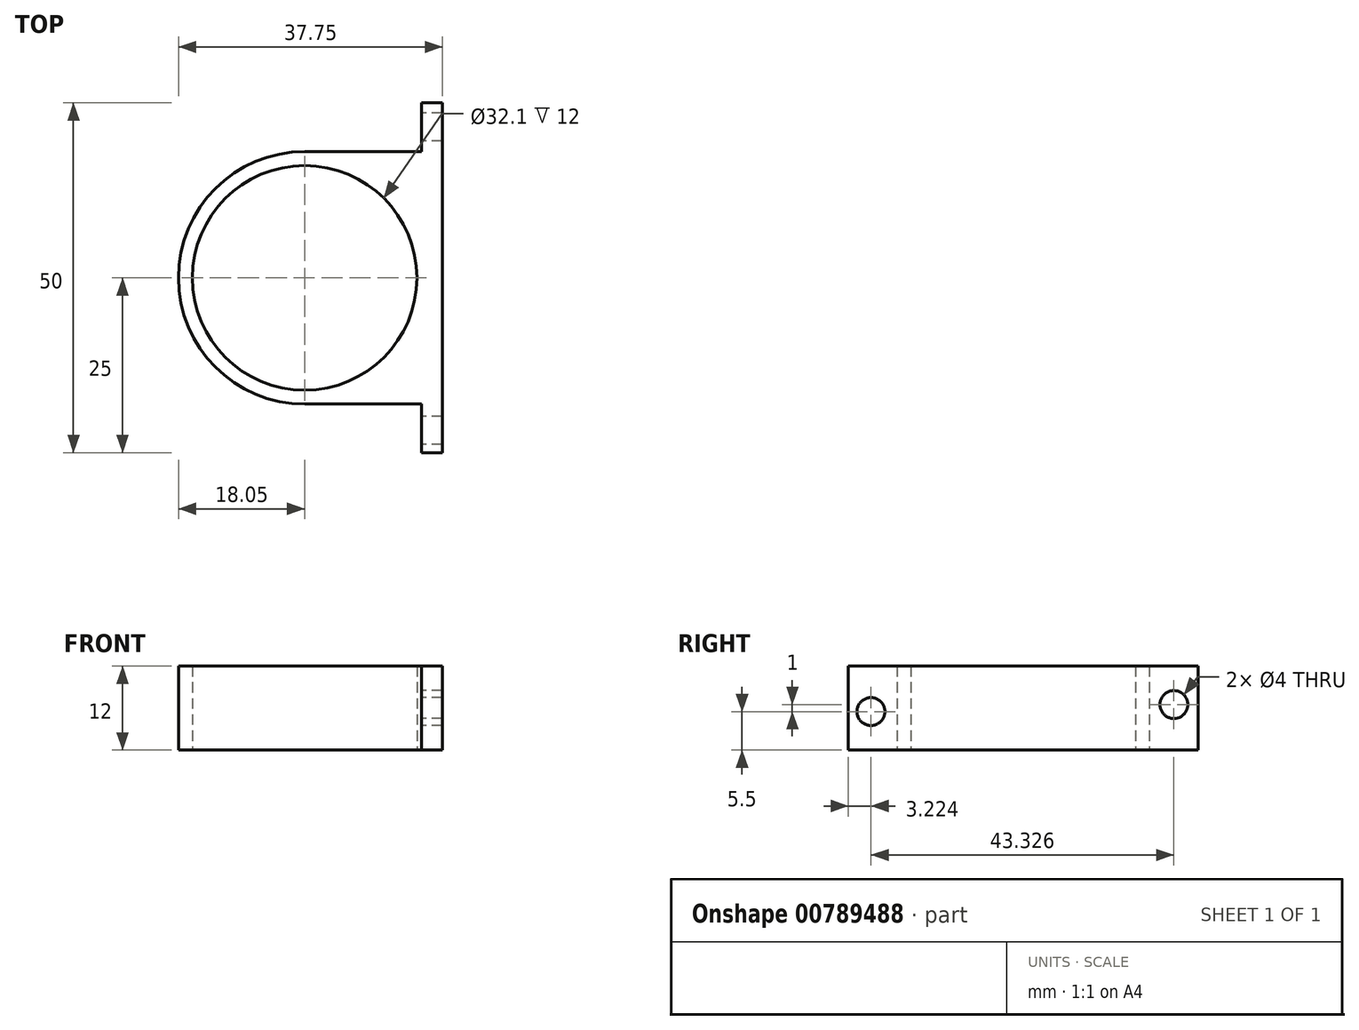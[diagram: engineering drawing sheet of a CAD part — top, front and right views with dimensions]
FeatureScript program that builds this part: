
annotation { "Feature Type Name" : "Feature", "Feature Type Description" : "" }
export const myFeature = defineFeature(function(context is Context, id is Id, definition is map)
    precondition{}
    {
        {
            var Q0;
            Q0=qCreatedBy(makeId("Top.planeOp"),FACE);
            var sketch = newSketch(context, id + "F0", { "sketchPlane" : qUnion([Q0])});
            skCircle(sketch, "E0", {"center": v(0, 0) * mm, "radius": 16.05 * mm});
            skCircle(sketch, "E1.0", {"center": v(0, 0) * mm, "radius": 18.05 * mm});
            skPoint(sketch, "E2", {"position": v(0, 18.05) * mm});
            skPoint(sketch, "E3", {"position": v(0, -18.05) * mm});
            skPoint(sketch, "E4", {"position": v(19.7, 0) * mm});
            skLineSegment(sketch, "E5", {"start": v(19.7, 0) * mm, "end": v(19.7, 25) * mm});
            skLineSegment(sketch, "E6", {"start": v(19.7, 25) * mm, "end": v(16.7, 25) * mm});
            skLineSegment(sketch, "E7", {"start": v(0, 18.05) * mm, "end": v(16.72, 18.05) * mm});
            skLineSegment(sketch, "E8", {"start": v(16.72, 18.05) * mm, "end": v(16.7, 25) * mm});
            skLineSegment(sketch, "E9.MirrorCS", {"start": v(19.7, 0) * mm, "end": v(19.7, -25) * mm});
            skLineSegment(sketch, "E10.MirrorCS", {"start": v(0, -18.05) * mm, "end": v(16.72, -18.05) * mm});
            skLineSegment(sketch, "E11.MirrorCS", {"start": v(16.72, -18.05) * mm, "end": v(16.7, -25) * mm});
            skLineSegment(sketch, "E12.MirrorCS", {"start": v(19.7, -25) * mm, "end": v(16.7, -25) * mm});
            skSolve(sketch);
        }
        {
            var Q0;
            Q0=makeQuery(id+"F0.imprint","IMPRINT",FACE,{"disambiguationData":[TD([[makeQuery(id+"F0.imprint","IMPRINT",EDGE,{"derivedFrom":sQuery(id+"F0.wireOp",EDGE,"E0")}),-1.0]])]});
            var Q1;
            Q1=makeQuery(id+"F0.imprint","IMPRINT",FACE,{"disambiguationData":[TD([[makeQuery(id+"F0.imprint","IMPRINT",EDGE,{"derivedFrom":sQuery(id+"F0.wireOp",EDGE,"E5")}),1.0]])]});
            extrude(context, id + "F1", {"entities" : qUnion([Q0, Q1]), "depth" : 12 * mm, "offsetDistance" : 25 * mm});
        }
        {
            var Q0;
            Q0=makeQuery(id+"F1.opExtrude","SWEPT_FACE",FACE,{"disambiguationData":[OSD([sQuery(id+"F0.wireOp",EDGE,"E11.MirrorCS")])]});
            var sketch = newSketch(context, id + "F2", { "sketchPlane" : qUnion([Q0])});
            skLineSegment(sketch, "E13.bottom", {"start": v(24.96, 0) * mm, "end": v(21.74, 0) * mm});
            skLineSegment(sketch, "E13.top", {"start": v(24.96, 5.5) * mm, "end": v(21.74, 5.5) * mm});
            skLineSegment(sketch, "E13.left", {"start": v(24.96, 0) * mm, "end": v(24.96, 5.5) * mm});
            skLineSegment(sketch, "E13.right", {"start": v(21.74, 0) * mm, "end": v(21.74, 5.5) * mm});
            skCircle(sketch, "E14", {"center": v(21.74, 5.5) * mm, "radius": 2 * mm});
            skSolve(sketch);
        }
        {
            var Q0;
            Q0=makeQuery(id+"F2.imprint","IMPRINT",FACE,{"disambiguationData":[TD([[makeQuery(id+"F2.imprint","IMPRINT",EDGE,{"derivedFrom":sQuery(id+"F2.wireOp",EDGE,"2011fcad-b65f-45e6-974c-2674e0ec2c9b0.MirrorC")}),-1.0]])]});
            var Q1;
            {var subQ0=sQuery(id+"F2.wireOp",EDGE,"E13.right");var subQ1=sQuery(id+"F2.wireOp",EDGE,"E13.top");var subQ2=makeQuery(id+"F2.imprint","INTERSECT",VERTEX,{"derivedFrom":[subQ1,subQ0]});Q1=makeQuery(id+"F2.imprint","IMPRINT",FACE,{"disambiguationData":[TD([[makeQuery(id+"F2.imprint","IMPRINT",EDGE,{"disambiguationData":[TD([[subQ2,1.0]])],"derivedFrom":subQ1}),-1.0]])]});}
            var Q2;
            {var subQ0=sQuery(id+"F2.wireOp",EDGE,"E13.right");var subQ1=sQuery(id+"F2.wireOp",EDGE,"E13.top");var subQ2=makeQuery(id+"F2.imprint","INTERSECT",VERTEX,{"derivedFrom":[subQ1,subQ0]});Q2=makeQuery(id+"F2.imprint","IMPRINT",FACE,{"disambiguationData":[TD([[makeQuery(id+"F2.imprint","IMPRINT",EDGE,{"disambiguationData":[TD([[subQ2,1.0]])],"derivedFrom":subQ1}),1.0]])]});}
            extrude(context, id + "F3", {"entities" : qUnion([Q0, Q1, Q2]), "operationType" : NewBodyOperationType.REMOVE, "oppositeDirection" : true, "depth" : 25 * mm, "offsetDistance" : 25 * mm});
        }
        {
            var Q0;
            Q0=makeQuery(id+"F1.opExtrude","SWEPT_FACE",FACE,{"disambiguationData":[OSD([sQuery(id+"F0.wireOp",EDGE,"E8")])]});
            var sketch = newSketch(context, id + "F4", { "sketchPlane" : qUnion([Q0])});
            skLineSegment(sketch, "E15.bottom", {"start": v(-24.96, 12) * mm, "end": v(-21.51, 12) * mm});
            skLineSegment(sketch, "E15.top", {"start": v(-24.96, 6.5) * mm, "end": v(-21.51, 6.5) * mm});
            skLineSegment(sketch, "E15.left", {"start": v(-24.96, 12) * mm, "end": v(-24.96, 6.5) * mm});
            skLineSegment(sketch, "E15.right", {"start": v(-21.51, 12) * mm, "end": v(-21.51, 6.5) * mm});
            skCircle(sketch, "E16", {"center": v(-21.51, 6.5) * mm, "radius": 2 * mm});
            skSolve(sketch);
        }
        {
            var Q0;
            {var subQ0=sQuery(id+"F4.wireOp",EDGE,"E15.right");var subQ1=sQuery(id+"F4.wireOp",EDGE,"E15.top");var subQ2=makeQuery(id+"F4.imprint","INTERSECT",VERTEX,{"derivedFrom":[subQ1,subQ0]});Q0=makeQuery(id+"F4.imprint","IMPRINT",FACE,{"disambiguationData":[TD([[makeQuery(id+"F4.imprint","IMPRINT",EDGE,{"disambiguationData":[TD([[subQ2,1.0]])],"derivedFrom":subQ1}),1.0]])]});}
            var Q1;
            {var subQ0=sQuery(id+"F4.wireOp",EDGE,"E15.right");var subQ1=sQuery(id+"F4.wireOp",EDGE,"E15.top");var subQ2=makeQuery(id+"F4.imprint","INTERSECT",VERTEX,{"derivedFrom":[subQ1,subQ0]});Q1=makeQuery(id+"F4.imprint","IMPRINT",FACE,{"disambiguationData":[TD([[makeQuery(id+"F4.imprint","IMPRINT",EDGE,{"disambiguationData":[TD([[subQ2,1.0]])],"derivedFrom":subQ1}),-1.0]])]});}
            extrude(context, id + "F5", {"entities" : qUnion([Q0, Q1]), "operationType" : NewBodyOperationType.REMOVE, "oppositeDirection" : true, "depth" : 25 * mm, "offsetDistance" : 25 * mm});
        }
    });
